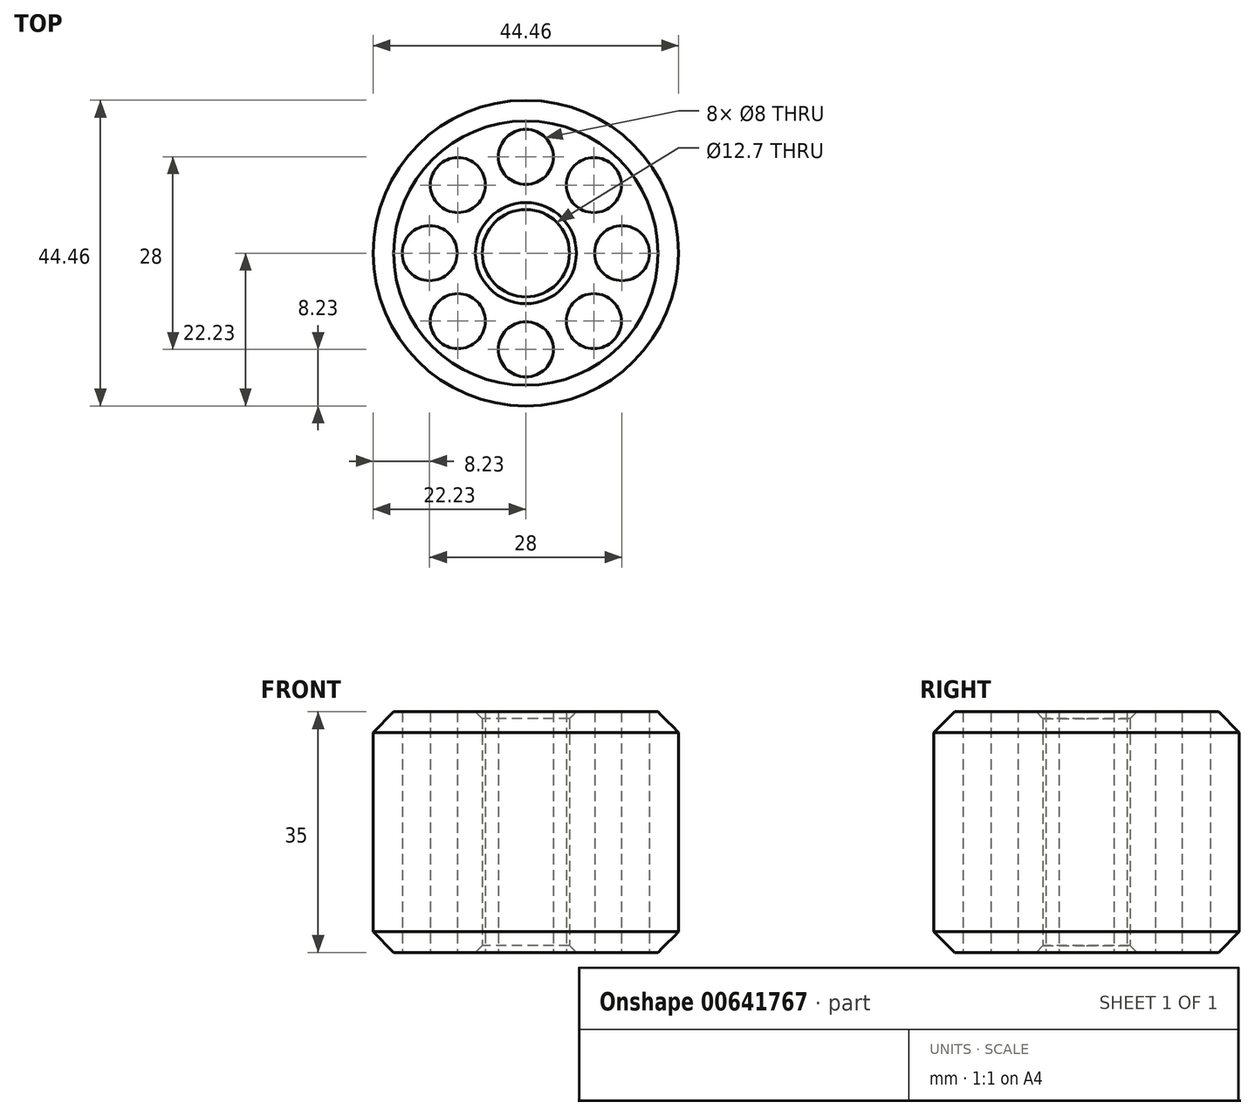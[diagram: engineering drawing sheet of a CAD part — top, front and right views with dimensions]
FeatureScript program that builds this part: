
annotation { "Feature Type Name" : "Feature", "Feature Type Description" : "" }
export const myFeature = defineFeature(function(context is Context, id is Id, definition is map)
    precondition{}
    {
        {
            var Q0;
            Q0=qCreatedBy(makeId("Top.planeOp"),FACE);
            var sketch = newSketch(context, id + "F0", { "sketchPlane" : qUnion([Q0])});
            skCircle(sketch, "E0", {"center": v(0, 0) * mm, "radius": 22.23 * mm});
            skCircle(sketch, "E1", {"center": v(0, 0) * mm, "radius": 6.35 * mm});
            skCircle(sketch, "E2", {"center": v(0, 0) * mm, "radius": 14 * mm, "construction": true});
            skCircle(sketch, "E3", {"center": v(14, 0) * mm, "radius": 4 * mm});
            skCircle(sketch, "E4.1.0", {"center": v(9.9, 9.9) * mm, "radius": 4 * mm});
            skCircle(sketch, "E4.2.0", {"center": v(0, 14) * mm, "radius": 4 * mm});
            skCircle(sketch, "E4.3.0", {"center": v(-9.9, 9.9) * mm, "radius": 4 * mm});
            skCircle(sketch, "E4.4.0", {"center": v(-14, 0) * mm, "radius": 4 * mm});
            skCircle(sketch, "E4.5.0", {"center": v(-9.9, -9.9) * mm, "radius": 4 * mm});
            skCircle(sketch, "E4.6.0", {"center": v(0, -14) * mm, "radius": 4 * mm});
            skCircle(sketch, "E4.7.0", {"center": v(9.9, -9.9) * mm, "radius": 4 * mm});
            skSolve(sketch);
        }
        {
            var Q0;
            Q0 = qSketchRegion(id + "F0", true);
            extrude(context, id + "F1", {"entities" : qUnion([Q0]), "depth" : 35 * mm, "offsetDistance" : 25 * mm});
        }
        {
            var Q0;
            Q0=makeQuery(id+"F1.opExtrude","CAP_EDGE",EDGE,{"disambiguationData":[OSD([sQuery(id+"F0.wireOp",EDGE,"E0")])],"isStart":false});
            var Q1;
            Q1=makeQuery(id+"F1.opExtrude","CAP_EDGE",EDGE,{"disambiguationData":[OSD([sQuery(id+"F0.wireOp",EDGE,"E0")])],"isStart":true});
            chamfer(context, id + "F2", {"entities" : qUnion([Q0, Q1]), "width" : 3 * mm, "tangentPropagation" : true});
        }
        {
            var Q0;
            Q0=makeQuery(id+"F1.opExtrude","CAP_EDGE",EDGE,{"disambiguationData":[OSD([sQuery(id+"F0.wireOp",EDGE,"E1")])],"isStart":true});
            var Q1;
            Q1=makeQuery(id+"F1.opExtrude","CAP_EDGE",EDGE,{"disambiguationData":[OSD([sQuery(id+"F0.wireOp",EDGE,"E1")])],"isStart":false});
            chamfer(context, id + "F3", {"entities" : qUnion([Q0, Q1]), "width" : 1 * mm, "tangentPropagation" : true});
        }
    });
